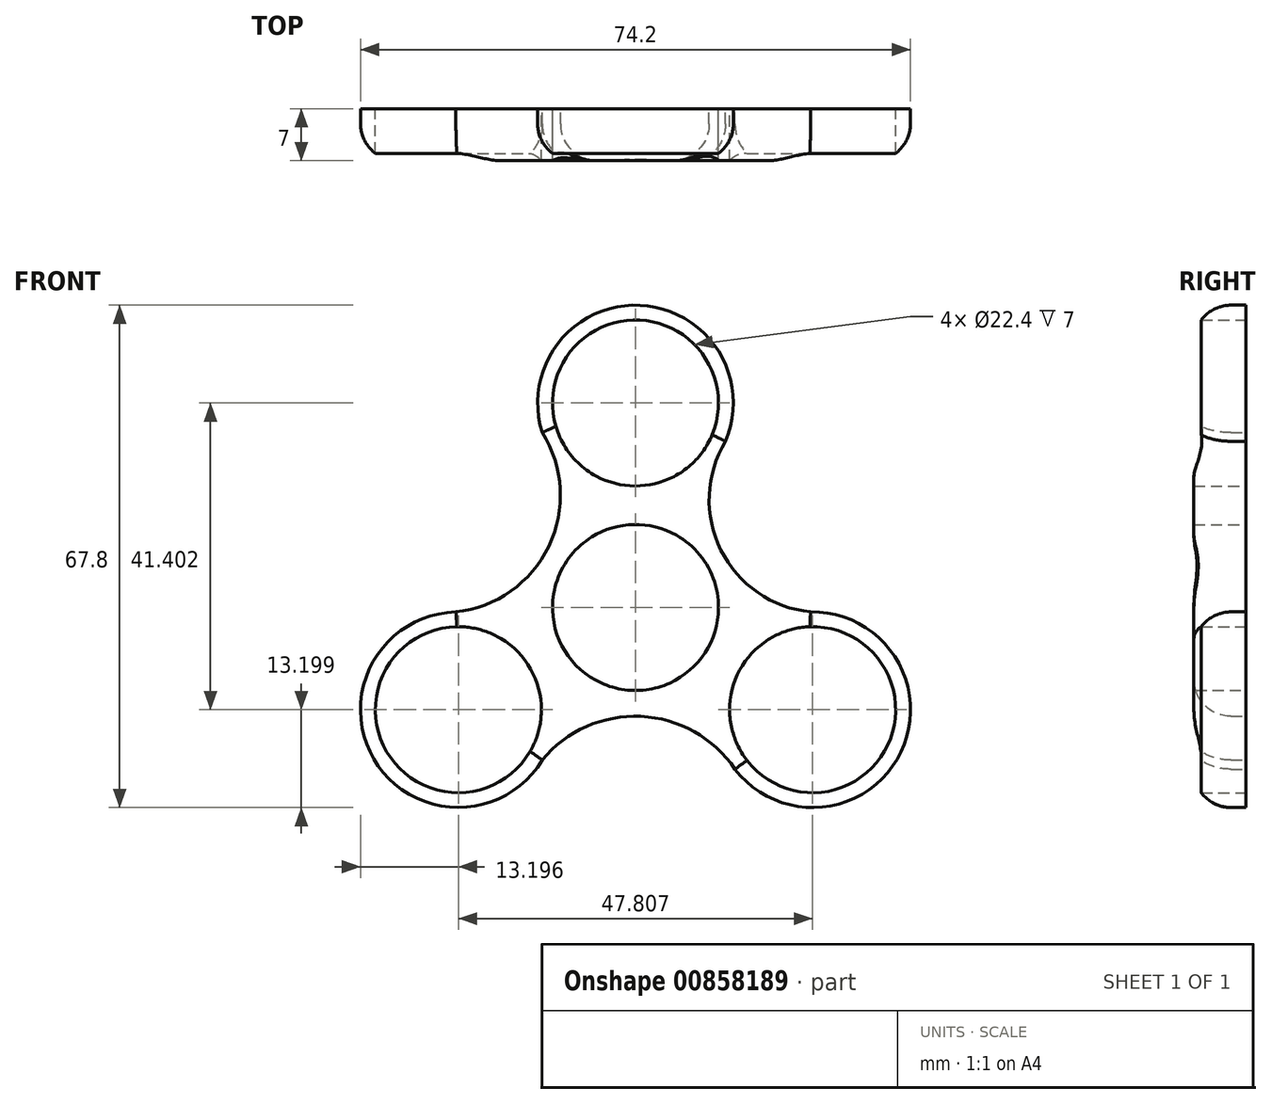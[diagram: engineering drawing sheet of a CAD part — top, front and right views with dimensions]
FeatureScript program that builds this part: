
annotation { "Feature Type Name" : "Feature", "Feature Type Description" : "" }
export const myFeature = defineFeature(function(context is Context, id is Id, definition is map)
    precondition{}
    {
        {
            var Q0;
            Q0=qCreatedBy(makeId("Front.planeOp"),FACE);
            var sketch = newSketch(context, id + "F0", { "sketchPlane" : qUnion([Q0])});
            skCircle(sketch, "E0", {"center": v(0, 0) * mm, "radius": 11.2 * mm});
            skCircle(sketch, "E1", {"center": v(0, 27.6) * mm, "radius": 11.2 * mm});
            skArc(sketch, "E2", {"start": v(11.2, 20.63) * mm, "mid": v(-0.2, 40.8) * mm, "end": v(-10.99, 20.29) * mm});
            skArc(sketch, "E3.1.0", {"start": v(-24.23, -0.6) * mm, "mid": v(-35.3, -20.45) * mm, "end": v(-12.58, -20.59) * mm});
            skCircle(sketch, "E3.1.1", {"center": v(-23.9, -13.8) * mm, "radius": 11.2 * mm});
            skArc(sketch, "E3.2.0", {"start": v(12.93, -21.14) * mm, "mid": v(35.62, -19.9) * mm, "end": v(23.6, -0.6) * mm});
            skCircle(sketch, "E3.2.1", {"center": v(23.9, -13.8) * mm, "radius": 11.2 * mm});
            skArc(sketch, "E4", {"start": v(12.14, 22.43) * mm, "mid": v(11.52, 7.75) * mm, "end": v(23.6, -0.6) * mm});
            skArc(sketch, "E5", {"start": v(13.42, -21.82) * mm, "mid": v(0.73, -14.7) * mm, "end": v(-12.58, -20.59) * mm});
            skArc(sketch, "E6", {"start": v(-24.23, -0.6) * mm, "mid": v(-11.7, 8.27) * mm, "end": v(-12.58, 23.6) * mm});
            skSolve(sketch);
        }
        {
            var Q0;
            Q0=makeQuery(id+"F0.imprint","IMPRINT",FACE,{"disambiguationData":[TD([[makeQuery(id+"F0.imprint","IMPRINT",EDGE,{"derivedFrom":sQuery(id+"F0.wireOp",EDGE,"E0")}),-1.0]])]});
            extrude(context, id + "F1", {"entities" : qUnion([Q0]), "depth" : 7 * mm, "offsetDistance" : 25 * mm});
        }
        {
            var Q0;
            Q0=makeQuery(id+"F1.opExtrude","CAP_EDGE",EDGE,{"disambiguationData":[OSD([sQuery(id+"F0.wireOp",EDGE,"E4")])],"isStart":false});
            var Q1;
            Q1=makeQuery(id+"F1.opExtrude","CAP_EDGE",EDGE,{"disambiguationData":[OSD([sQuery(id+"F0.wireOp",EDGE,"E6")])],"isStart":false});
            var Q2;
            Q2=makeQuery(id+"F1.opExtrude","CAP_EDGE",EDGE,{"disambiguationData":[OSD([sQuery(id+"F0.wireOp",EDGE,"E5")])],"isStart":false});
            var Q3;
            Q3=makeQuery(id+"F1.opExtrude","CAP_EDGE",EDGE,{"disambiguationData":[OSD([sQuery(id+"F0.wireOp",EDGE,"E2")])],"isStart":false});
            var Q4;
            Q4=makeQuery(id+"F1.opExtrude","CAP_EDGE",EDGE,{"disambiguationData":[OSD([sQuery(id+"F0.wireOp",EDGE,"E3.2.0")])],"isStart":false});
            var Q5;
            Q5=makeQuery(id+"F1.opExtrude","CAP_EDGE",EDGE,{"disambiguationData":[OSD([sQuery(id+"F0.wireOp",EDGE,"E3.1.0")])],"isStart":false});
            fillet(context, id + "F2", {"entities" : qUnion([Q0, Q1, Q2, Q3, Q4, Q5]), "radius" : 5 * mm, "tangentPropagation" : true, "allowEdgeOverflow" : false});
        }
    });
